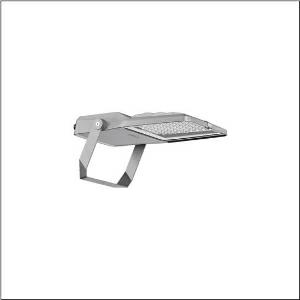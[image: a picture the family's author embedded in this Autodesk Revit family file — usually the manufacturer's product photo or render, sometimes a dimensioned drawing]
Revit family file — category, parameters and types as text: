
# Revit family: floodlight_fl_21_mini___pl64_5xa7772b5e1a_ffc6
name_source: partatom
category: Lighting Fixtures
units: mm (PartAtom-declared; Revit-internal decimal feet)

## family parameters
Cut with Voids When Loaded = No
Host = Face
Light Source = No
Part Type = Normal
Room Calculation Point = No
Round Connector Dimension = Use Diameter
Shared = No

## types (1)
- --- (1 x LED, 5620 lm, 45.5 W, 4000K)
    Apparent Load = 46 VA
    CIE Flux Codes = 28 80 98 100 100
    Color Rendering = 80
    Color Temperature = 4000K
    Default Elevation = 1800 mm
    Description = Floodlight FL 21 mini, floodlight, primary light control with lens, of PMMA, primary optical cover: protective disc, of toughened safety glass, transparent, light distribution: PL64, light emission: direct distribution, installation type: surface-mounted, LED, High Power LED, rated luminous flux: 5.620lm, luminous efficacy: 124lm/W, light colour: 840, colour temperature: 4000K, control gear: ECG iQ, control: Street-Remote, Auto-Match, Temp-Guard, Night-Set, Smart-Wire, Desk-Remote (wireless, voltage-free reading and setting of iQ features in the workshop via application-optimized NFC function/RFID function), optimised constant luminous flux control (CLO 2.0), with terminal, 6-pole, mains connection: 220..240V, AC, 50/60Hz, start of lifetime: 46W, end of lifetime: 48W, reduction: 22W, luminaire housing, of diecast aluminium, powder-coated, Siteco® metallic grey (DB 702S), corrosivity category C5 according to DIN EN ISO 12944, mounting bracket, of steel, galvanised, powder-coated, Siteco® metallic grey (DB 702S), protection rating (complete): IP66, insulation class (complete): insulation class II (safety insulation), certification: CE, ENEC, VDE, protection symbol: D, impact resistance: IK08, permissible operating ambient temperature: -40..+40°C, permissible operating ambient temperature for outdoor applications: -40..+50°C, standard: DIN EN 12944, packaging unit: 1 piece

Light Distribution: PL64
    Height = 70 mm
    Lamp = 1 x LED
    Lamp Light Flux = 5620 lm
    Lamp Power = 45.5 W
    Lamp count = 1
    Length = 485 mm
    Luminous efficacy = 124 lm/W
    Manufacturer = Siteco
    ModVariant = No
    Model = 5XA7772B5E1A
    Number of Poles = 1
    OnlyDefault = Yes
    Power Factor = 1
    Product Name = Floodlight FL 21 mini | PL64
    Product group = floodlight | pylon top
    ProductGroupID = 6101
    Protection Class = Protection class II
    Protection Degree = IP 66
    RLX_Detail_Level = 1
    RlxData = <blob elided: 95917 chars, md5=c442a1f7>
    Socket = socket
    Standby Power = 0 W
    System Light Flux = 5620 lm
    System Power = 46 W
    Type Comments = factory setting: luminous flux: 100 % | dim-lin: 254 | 463 mA
    Type Image = l_1006845.jpg
    URL = http://relux.com
    VarID = @adj_077773
    Voltage = 0 V
    Weight = 0.00 kg
    Width = 337 mm

## geometry (parser evidence)
native form markers: Blend x4, Sweep x12
no freeform markers — native parametric forms only
